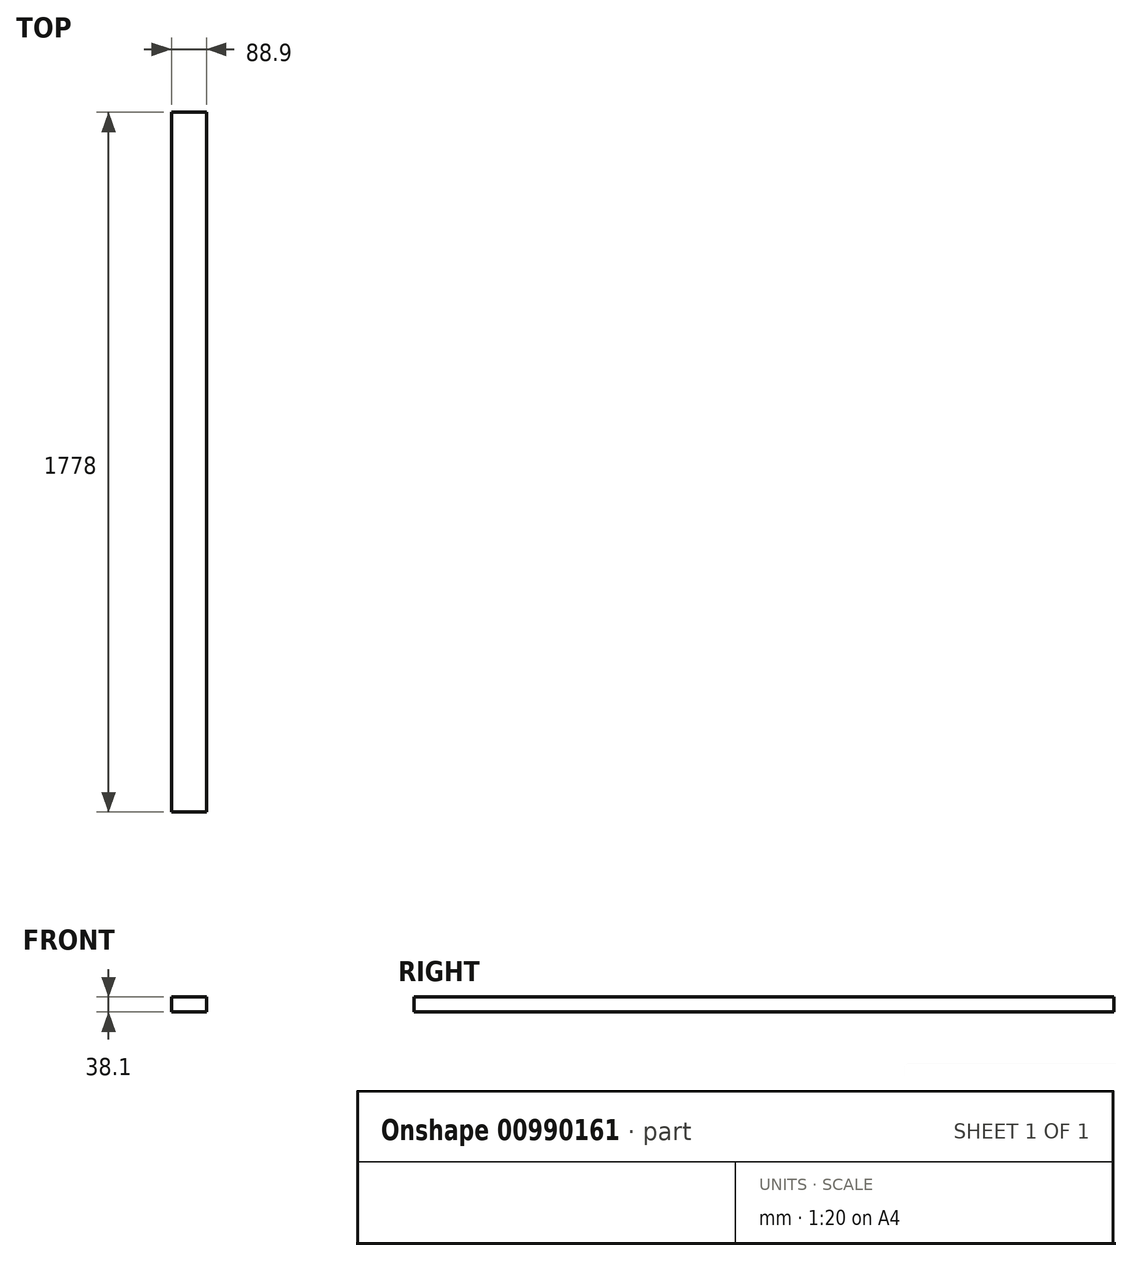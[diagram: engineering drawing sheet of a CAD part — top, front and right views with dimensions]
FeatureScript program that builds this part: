
annotation { "Feature Type Name" : "Feature", "Feature Type Description" : "" }
export const myFeature = defineFeature(function(context is Context, id is Id, definition is map)
    precondition{}
    {
        {
            assignVariable(context, id + "F0", {"name" : "w", "anyValue" : 38.1 * mm});
        }
        {
            var Q0;
            Q0=qCreatedBy(makeId("Top.planeOp"),FACE);
            var sketch = newSketch(context, id + "F1", { "sketchPlane" : qUnion([Q0])});
            skLineSegment(sketch, "E0.bottom", {"start": v(44.45, 889) * mm, "end": v(-44.45, 889) * mm});
            skLineSegment(sketch, "E0.top", {"start": v(44.45, -889) * mm, "end": v(-44.45, -889) * mm});
            skLineSegment(sketch, "E0.left", {"start": v(44.45, 889) * mm, "end": v(44.45, -889) * mm});
            skLineSegment(sketch, "E0.right", {"start": v(-44.45, 889) * mm, "end": v(-44.45, -889) * mm});
            skPoint(sketch, "E0.middle", {"position": v(0, 0) * mm});
            skSolve(sketch);
        }
        {
            var Q0;
            Q0=qSketchRegion(id+"F1",true);
            extrude(context, id + "F2", {"entities" : qUnion([Q0]), "depth" : getVariable(context, 'w'), "offsetDistance" : 25.4 * mm});
        }
    });
